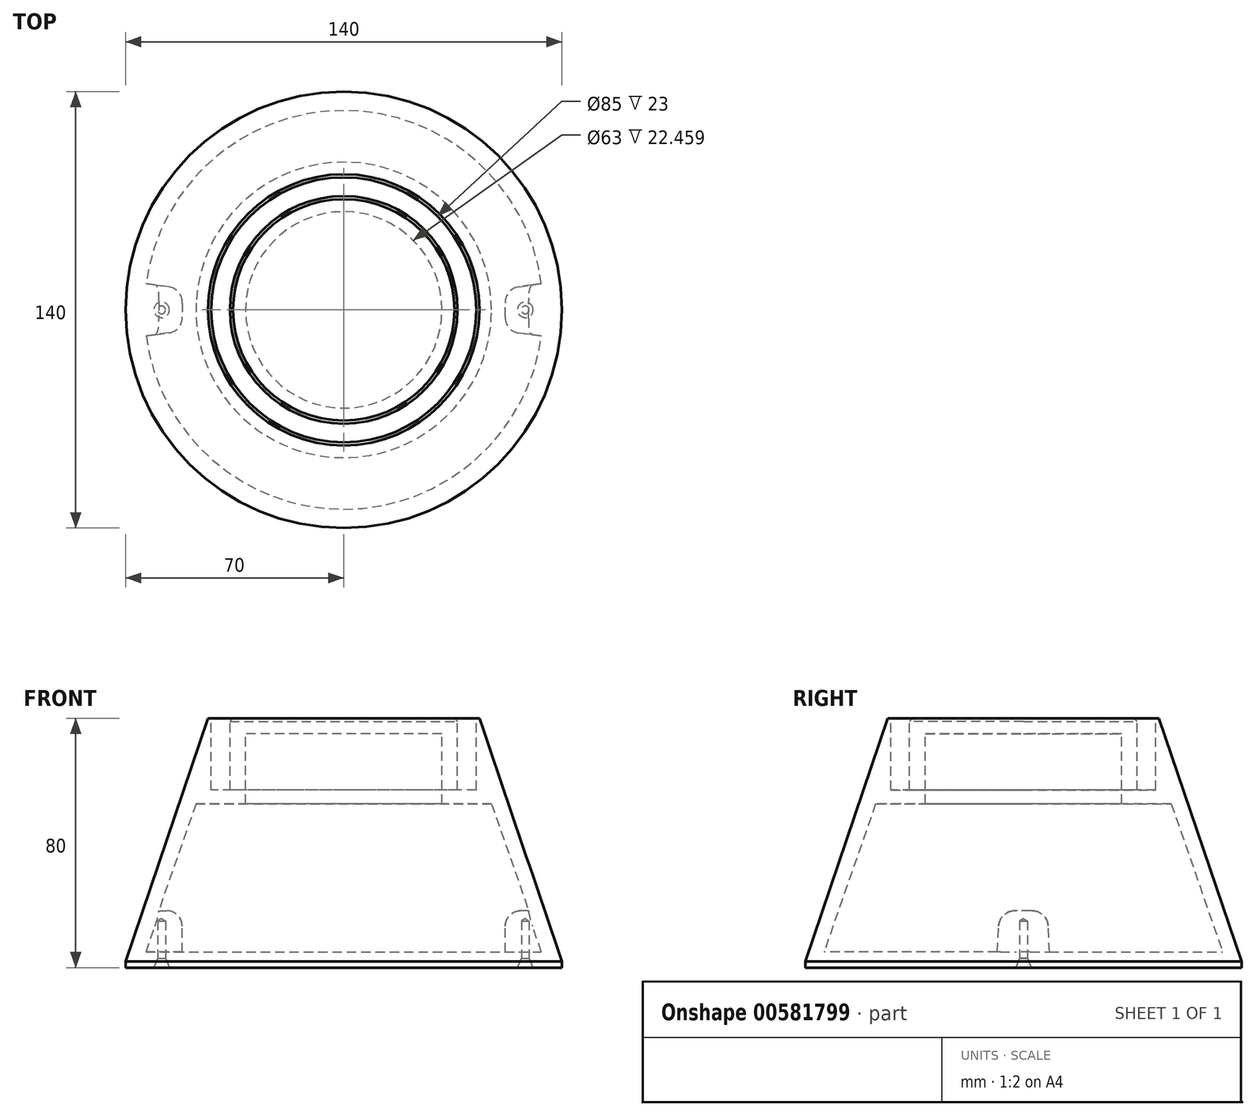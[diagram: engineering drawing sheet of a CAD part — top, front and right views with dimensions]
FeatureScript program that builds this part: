
annotation { "Feature Type Name" : "Feature", "Feature Type Description" : "" }
export const myFeature = defineFeature(function(context is Context, id is Id, definition is map)
    precondition{}
    {
        {
            var Q0;
            Q0=qCreatedBy(makeId("Front.planeOp"),FACE);
            var sketch = newSketch(context, id + "F0", { "sketchPlane" : qUnion([Q0])});
            skLineSegment(sketch, "E0.bottom", {"start": v(43.5, 80) * mm, "end": v(42.5, 80) * mm});
            skLineSegment(sketch, "E0.top", {"start": v(70, 0) * mm, "end": v(0, 0) * mm});
            skLineSegment(sketch, "E0.left", {"start": v(70, 2) * mm, "end": v(70, 0) * mm});
            skLineSegment(sketch, "E1", {"start": v(70, 2) * mm, "end": v(43.5, 80) * mm});
            skLineSegment(sketch, "E2", {"start": v(42.5, 80) * mm, "end": v(42.5, 57) * mm});
            skLineSegment(sketch, "E3", {"start": v(42.5, 57) * mm, "end": v(36.5, 57) * mm});
            skLineSegment(sketch, "E4", {"start": v(36.5, 57) * mm, "end": v(36.5, 80) * mm});
            skLineSegment(sketch, "E5", {"start": v(36.5, 80) * mm, "end": v(0, 80) * mm});
            skLineSegment(sketch, "E6", {"start": v(0, 80) * mm, "end": v(0, 0) * mm});
            skLineSegment(sketch, "E7", {"start": v(65, 0) * mm, "end": v(65, 2) * mm});
            skLineSegment(sketch, "E8", {"start": v(65, 2) * mm, "end": v(47.41, 52.54) * mm});
            skLineSegment(sketch, "E9", {"start": v(36.5, 80) * mm, "end": v(31.5, 80) * mm});
            skLineSegment(sketch, "E10", {"start": v(31.5, 75) * mm, "end": v(31.5, 57) * mm});
            skLineSegment(sketch, "E11", {"start": v(31.5, 57) * mm, "end": v(31.5, 52.54) * mm});
            skLineSegment(sketch, "E12", {"start": v(31.5, 52.54) * mm, "end": v(47.41, 52.54) * mm});
            skPoint(sketch, "E13.orphan", {"position": v(45.86, 57) * mm});
            skLineSegment(sketch, "E14", {"start": v(31.5, 75) * mm, "end": v(0, 75) * mm});
            skPoint(sketch, "E15.orphan", {"position": v(70, 80) * mm});
            skLineSegment(sketch, "E16", {"start": v(0, 5) * mm, "end": v(63.96, 5) * mm});
            skLineSegment(sketch, "E17", {"start": v(59.35, 18.24) * mm, "end": v(51.83, 18.24) * mm});
            skLineSegment(sketch, "E18", {"start": v(51.83, 18.24) * mm, "end": v(51.83, 5) * mm});
            skPoint(sketch, "E19.orphan", {"position": v(-70, 80) * mm});
            skPoint(sketch, "E20.orphan", {"position": v(-70, 0) * mm});
            skLineSegment(sketch, "E21.MirrorCS", {"start": v(-43.5, 80) * mm, "end": v(-42.5, 80) * mm});
            skLineSegment(sketch, "E22.MirrorCS", {"start": v(-65, 0) * mm, "end": v(-65, 2) * mm});
            skLineSegment(sketch, "E23.MirrorCS", {"start": v(-42.5, 57) * mm, "end": v(-36.5, 57) * mm});
            skLineSegment(sketch, "E24.MirrorCS", {"start": v(-31.5, 57) * mm, "end": v(-31.5, 52.54) * mm});
            skLineSegment(sketch, "E25.MirrorCS", {"start": v(-70, 2) * mm, "end": v(-70, 0) * mm});
            skLineSegment(sketch, "E26.MirrorCS", {"start": v(-36.5, 80) * mm, "end": v(-31.5, 80) * mm});
            skLineSegment(sketch, "E27.MirrorCS", {"start": v(-36.5, 80) * mm, "end": v(0, 80) * mm});
            skLineSegment(sketch, "E28.MirrorCS", {"start": v(-31.5, 52.54) * mm, "end": v(-47.41, 52.54) * mm});
            skLineSegment(sketch, "E29.MirrorCS", {"start": v(-65, 2) * mm, "end": v(-47.41, 52.54) * mm});
            skLineSegment(sketch, "E30.MirrorCS", {"start": v(-36.5, 57) * mm, "end": v(-36.5, 80) * mm});
            skLineSegment(sketch, "E31.MirrorCS", {"start": v(0, 5) * mm, "end": v(-63.96, 5) * mm});
            skLineSegment(sketch, "E32.MirrorCS", {"start": v(-70, 2) * mm, "end": v(-43.5, 80) * mm});
            skLineSegment(sketch, "E33.MirrorCS", {"start": v(-42.5, 80) * mm, "end": v(-42.5, 57) * mm});
            skPoint(sketch, "E34.MirrorP", {"position": v(-45.86, 57) * mm});
            skLineSegment(sketch, "E35.MirrorCS", {"start": v(-31.5, 75) * mm, "end": v(-31.5, 57) * mm});
            skLineSegment(sketch, "E36.MirrorCS", {"start": v(-70, 0) * mm, "end": v(0, 0) * mm});
            skLineSegment(sketch, "E37.MirrorCS", {"start": v(-59.35, 18.24) * mm, "end": v(-51.83, 18.24) * mm});
            skLineSegment(sketch, "E38.MirrorCS", {"start": v(-51.83, 18.24) * mm, "end": v(-51.83, 5) * mm});
            skLineSegment(sketch, "E39.MirrorCS", {"start": v(-31.5, 75) * mm, "end": v(0, 75) * mm});
            skSolve(sketch);
        }
        {
            var Q0;
            {var subQ6=sQuery(id+"F0.wireOp",EDGE,"E0.left");Q0=makeQuery(id+"F0.imprint","IMPRINT",FACE,{"disambiguationData":[TD([[makeQuery(id+"F0.imprint","IMPRINT",EDGE,{"derivedFrom":subQ6}),-1.0]])]});}
            var Q1;
            Q1=sQuery(id+"F0.wireOp",EDGE,"E6");
            revolve(context, id + "F1", {"entities" : qUnion([Q0]), "axis" : qUnion([Q1]), "revolveType" : RevolveType.FULL});
        }
        {
            var Q0;
            Q0=makeQuery(id+"F1.opRevolve","SWEPT_EDGE",EDGE,{"disambiguationData":[OSD([sQuery(id+"F0.wireOp",EDGE,"E4"),sQuery(id+"F0.wireOp",EDGE,"E5")])]});
            chamfer(context, id + "F2", {"entities" : qUnion([Q0]), "width" : 1 * mm, "tangentPropagation" : true});
        }
        {
            var Q0;
            {var subQ1=sQuery(id+"F0.wireOp",EDGE,"E7");Q0=makeQuery(id+"F0.imprint","IMPRINT",FACE,{"disambiguationData":[TD([[makeQuery(id+"F0.imprint","IMPRINT",EDGE,{"derivedFrom":subQ1}),1.0]])]});}
            var Q1;
            Q1=sQuery(id+"F0.wireOp",EDGE,"E6");
            revolve(context, id + "F3", {"entities" : qUnion([Q0]), "axis" : qUnion([Q1]), "revolveType" : RevolveType.FULL});
        }
        {
            var Q0;
            {var subQ3=sQuery(id+"F0.wireOp",EDGE,"E17");Q0=makeQuery(id+"F0.imprint","IMPRINT",FACE,{"disambiguationData":[TD([[makeQuery(id+"F0.imprint","IMPRINT",EDGE,{"derivedFrom":subQ3}),1.0]])]});}
            var Q1;
            Q1=sQuery(id+"F0.wireOp",EDGE,"E6");
            revolve(context, id + "F4", {"operationType" : NewBodyOperationType.ADD, "entities" : qUnion([Q0]), "axis" : qUnion([Q1]), "revolveType" : RevolveType.SYMMETRIC, "angle" : 15 * degree});
        }
        {
            var Q0;
            {var subQ3=sQuery(id+"F0.wireOp",EDGE,"E37.MirrorCS");Q0=makeQuery(id+"F0.imprint","IMPRINT",FACE,{"disambiguationData":[TD([[makeQuery(id+"F0.imprint","IMPRINT",EDGE,{"derivedFrom":subQ3}),-1.0]])]});}
            var Q1;
            Q1=sQuery(id+"F0.wireOp",EDGE,"E6");
            revolve(context, id + "F5", {"operationType" : NewBodyOperationType.ADD, "entities" : qUnion([Q0]), "axis" : qUnion([Q1]), "revolveType" : RevolveType.SYMMETRIC, "angle" : 15 * degree});
        }
        {
            var Q0;
            Q0=makeQuery(id+"F1.opRevolve","SWEPT_FACE",FACE,{"disambiguationData":[OSD([sQuery(id+"F0.wireOp",EDGE,"E0.top")])]});
            var sketch = newSketch(context, id + "F6", { "sketchPlane" : qUnion([Q0])});
            skPoint(sketch, "E40", {"position": v(58.23, 0) * mm});
            skPoint(sketch, "E41", {"position": v(-58.43, 0) * mm});
            skSolve(sketch);
        }
        {
            var Q0;
            Q0=sQuery(id+"F6.wireOp",VERTEX,"E40");
            var Q1;
            Q1=sQuery(id+"F6.wireOp",VERTEX,"E41");
            var Q2;
            Q2=makeQuery(id+"F1.opRevolve","SWEPT_BODY",BODY,{"disambiguationData":[OSD([sQuery(id+"F0.wireOp",EDGE,"E0.top"),sQuery(id+"F0.wireOp",EDGE,"E0.left"),sQuery(id+"F0.wireOp",EDGE,"E1"),sQuery(id+"F0.wireOp",EDGE,"E0.bottom"),sQuery(id+"F0.wireOp",EDGE,"E2"),sQuery(id+"F0.wireOp",EDGE,"E3"),sQuery(id+"F0.wireOp",EDGE,"E4"),sQuery(id+"F0.wireOp",EDGE,"E6"),sQuery(id+"F0.wireOp",EDGE,"E7"),sQuery(id+"F0.wireOp",EDGE,"E8"),sQuery(id+"F0.wireOp",EDGE,"E10"),sQuery(id+"F0.wireOp",EDGE,"E11"),sQuery(id+"F0.wireOp",EDGE,"E12"),sQuery(id+"F0.wireOp",EDGE,"E14"),sQuery(id+"F0.wireOp",EDGE,"E5")])]});
            var Q3;
            Q3=makeQuery(id+"F3.opRevolve","SWEPT_BODY",BODY,{"disambiguationData":[OSD([sQuery(id+"F0.wireOp",EDGE,"E0.top"),sQuery(id+"F0.wireOp",EDGE,"E6"),sQuery(id+"F0.wireOp",EDGE,"E7"),sQuery(id+"F0.wireOp",EDGE,"E8"),sQuery(id+"F0.wireOp",EDGE,"E16")])]});
            hole(context, id + "F7", {"style" : HoleStyle.C_SINK, "endStyle" : HoleEndStyle.BLIND, "holeDiameter" : 2.5 * mm, "cSinkDiameter" : 5 * mm, "cSinkAngle" : 45 * degree, "majorDiameter" : 5 * mm, "holeDepth" : 15 * mm, "isTappedThrough" : true, "tappedDepth" : 7 * mm, "tapClearance" : 3, "startFromSketch" : true, "locations" : qUnion([Q0, Q1]), "scope" : qUnion([Q2, Q3])});
        }
        {
            var Q0;
            Q0=makeQuery(id+"F5.opRevolve","CAP_EDGE",EDGE,{"disambiguationData":[OSD([sQuery(id+"F0.wireOp",EDGE,"E38.MirrorCS")])],"isStart":true});
            var Q1;
            Q1=makeQuery(id+"F5.opRevolve","CAP_EDGE",EDGE,{"disambiguationData":[OSD([sQuery(id+"F0.wireOp",EDGE,"E38.MirrorCS")])],"isStart":false});
            var Q2;
            Q2=makeQuery(id+"F4.opRevolve","CAP_EDGE",EDGE,{"disambiguationData":[OSD([sQuery(id+"F0.wireOp",EDGE,"E18")])],"isStart":false});
            var Q3;
            Q3=makeQuery(id+"F4.opRevolve","CAP_EDGE",EDGE,{"disambiguationData":[OSD([sQuery(id+"F0.wireOp",EDGE,"E18")])],"isStart":true});
            var Q4;
            Q4=makeQuery(id+"F5.opRevolve","SWEPT_EDGE",EDGE,{"disambiguationData":[OSD([sQuery(id+"F0.wireOp",EDGE,"E37.MirrorCS"),sQuery(id+"F0.wireOp",EDGE,"E38.MirrorCS")])]});
            var Q5;
            Q5=makeQuery(id+"F4.opRevolve","SWEPT_EDGE",EDGE,{"disambiguationData":[OSD([sQuery(id+"F0.wireOp",EDGE,"E17"),sQuery(id+"F0.wireOp",EDGE,"E18")])]});
            var Q6;
            Q6=makeQuery(id+"F4.opRevolve","CAP_EDGE",EDGE,{"disambiguationData":[OSD([sQuery(id+"F0.wireOp",EDGE,"E17")])],"isStart":true});
            var Q7;
            Q7=makeQuery(id+"F4.opRevolve","CAP_EDGE",EDGE,{"disambiguationData":[OSD([sQuery(id+"F0.wireOp",EDGE,"E17")])],"isStart":false});
            var Q8;
            Q8=makeQuery(id+"F5.opRevolve","CAP_EDGE",EDGE,{"disambiguationData":[OSD([sQuery(id+"F0.wireOp",EDGE,"E37.MirrorCS")])],"isStart":true});
            var Q9;
            Q9=makeQuery(id+"F5.opRevolve","CAP_EDGE",EDGE,{"disambiguationData":[OSD([sQuery(id+"F0.wireOp",EDGE,"E37.MirrorCS")])],"isStart":false});
            fillet(context, id + "F8", {"entities" : qUnion([Q0, Q1, Q2, Q3, Q4, Q5, Q6, Q7, Q8, Q9]), "radius" : 5 * mm, "tangentPropagation" : true, "allowEdgeOverflow" : false});
        }
    });
